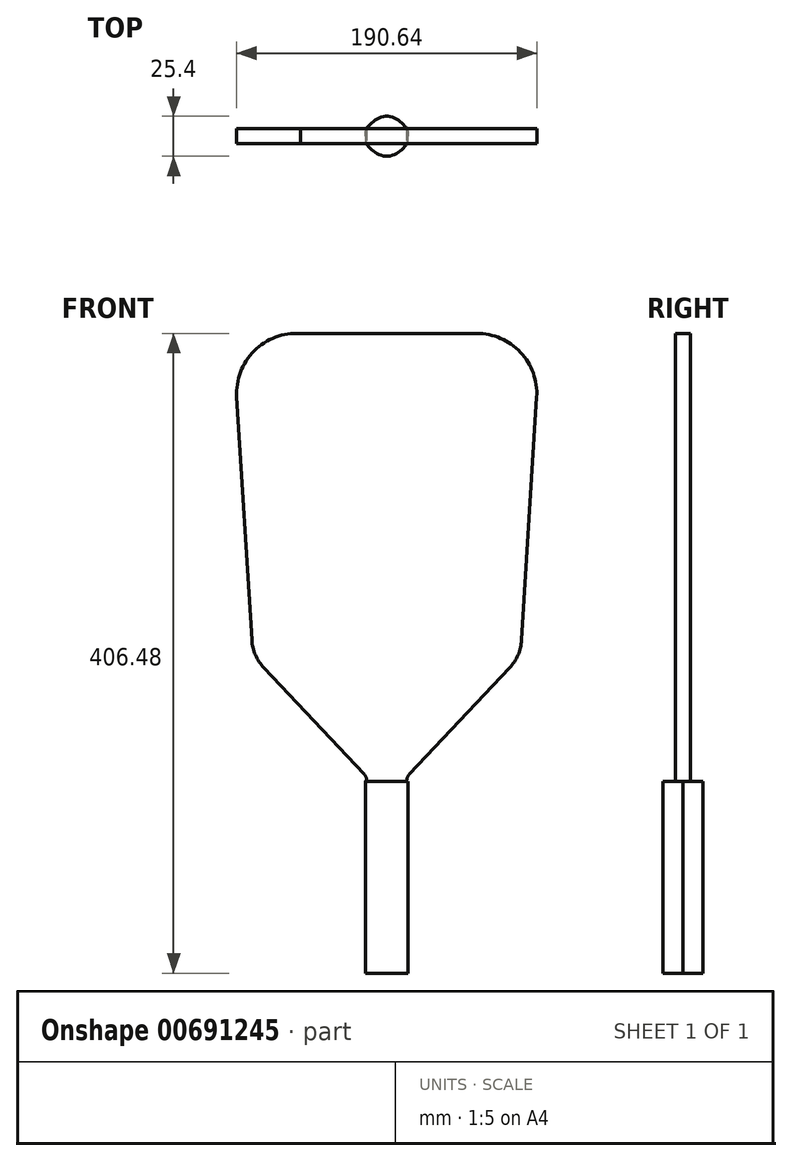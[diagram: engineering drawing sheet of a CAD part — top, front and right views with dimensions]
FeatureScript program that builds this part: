
annotation { "Feature Type Name" : "Feature", "Feature Type Description" : "" }
export const myFeature = defineFeature(function(context is Context, id is Id, definition is map)
    precondition{}
    {
        {
            var Q0;
            Q0=qCreatedBy(makeId("Front.planeOp"),FACE);
            var sketch = newSketch(context, id + "F0", { "sketchPlane" : qUnion([Q0])});
            skLineSegment(sketch, "E0", {"start": v(-65.02, -199.82) * mm, "end": v(-65.02, -77.63) * mm});
            skLineSegment(sketch, "E1.MirrorCS", {"start": v(-90.42, -199.82) * mm, "end": v(-90.42, -77.63) * mm});
            skLineSegment(sketch, "E2", {"start": v(-172.97, 166.2) * mm, "end": v(-163.39, 11.93) * mm});
            skLineSegment(sketch, "E3.MirrorCS", {"start": v(17.53, 166.2) * mm, "end": v(7.95, 11.93) * mm});
            skLineSegment(sketch, "E4", {"start": v(-92.15, -73.27) * mm, "end": v(-155.66, -5.9) * mm});
            skLineSegment(sketch, "E5.MirrorCS", {"start": v(-63.3, -73.27) * mm, "end": v(0.22, -5.9) * mm});
            skLineSegment(sketch, "E6", {"start": v(-132.58, 206.58) * mm, "end": v(-20.5, 206.58) * mm});
            skPoint(sketch, "E7.visualSharp", {"position": v(-90.42, -75.1) * mm});
            skArc(sketch, "E7.filletArc", {"start": v(-90.42, -77.63) * mm, "mid": v(-90.87, -75.28) * mm, "end": v(-92.15, -73.27) * mm});
            skPoint(sketch, "E8.visualSharp", {"position": v(-65.02, -75.1) * mm});
            skArc(sketch, "E8.filletArc", {"start": v(-63.3, -73.27) * mm, "mid": v(-64.57, -75.28) * mm, "end": v(-65.02, -77.63) * mm});
            skLineSegment(sketch, "E9", {"start": v(-90.42, -199.82) * mm, "end": v(-65.02, -199.82) * mm});
            skArc(sketch, "E10", {"start": v(-132.58, 206.58) * mm, "mid": v(-161.88, 195.5) * mm, "end": v(-172.97, 166.2) * mm});
            skArc(sketch, "E11", {"start": v(17.53, 166.2) * mm, "mid": v(7.24, 194.6) * mm, "end": v(-20.5, 206.58) * mm});
            skArc(sketch, "E12", {"start": v(-163.39, 11.93) * mm, "mid": v(-161.09, 2.33) * mm, "end": v(-155.66, -5.9) * mm});
            skArc(sketch, "E13", {"start": v(0.22, -5.9) * mm, "mid": v(5.65, 2.33) * mm, "end": v(7.95, 11.93) * mm});
            skSolve(sketch);
        }
        {
            var Q0;
            Q0 = qSketchRegion(id + "F0", true);
            extrude(context, id + "F1", {"entities" : qUnion([Q0]), "depth" : 9.52 * mm, "offsetDistance" : 25.4 * mm});
        }
        {
            var Q0;
            Q0=makeQuery(id+"F1.opExtrude","SWEPT_FACE",FACE,{"disambiguationData":[OSD([sQuery(id+"F0.wireOp",EDGE,"E9")])]});
            var sketch = newSketch(context, id + "F2", { "sketchPlane" : qUnion([Q0])});
            skFitSpline(sketch, "E14", {"points": [v(-91.28, 4.76) * mm, v(-90.42, 9.52) * mm, v(-77.72, 17.46) * mm, v(-65.02, 9.53) * mm, v(-64.16, 4.76) * mm], "startDerivative": vector(-1.6, 23.9) * mm, "endDerivative": vector(-1.6, -23.9) * mm});
            skFitSpline(sketch, "E15.MirrorCS", {"points": [v(-91.28, 4.76) * mm, v(-90.42, 0) * mm, v(-77.72, -7.94) * mm, v(-65.02, 0) * mm, v(-64.16, 4.76) * mm], "startDerivative": vector(-1.6, -23.9) * mm, "endDerivative": vector(-1.6, 23.9) * mm});
            skSolve(sketch);
        }
        {
            var Q0;
            Q0 = qSketchRegion(id + "F2", true);
            extrude(context, id + "F3", {"entities" : qUnion([Q0]), "operationType" : NewBodyOperationType.ADD, "oppositeDirection" : true, "depth" : 121.92 * mm, "offsetDistance" : 25.4 * mm});
        }
    });
